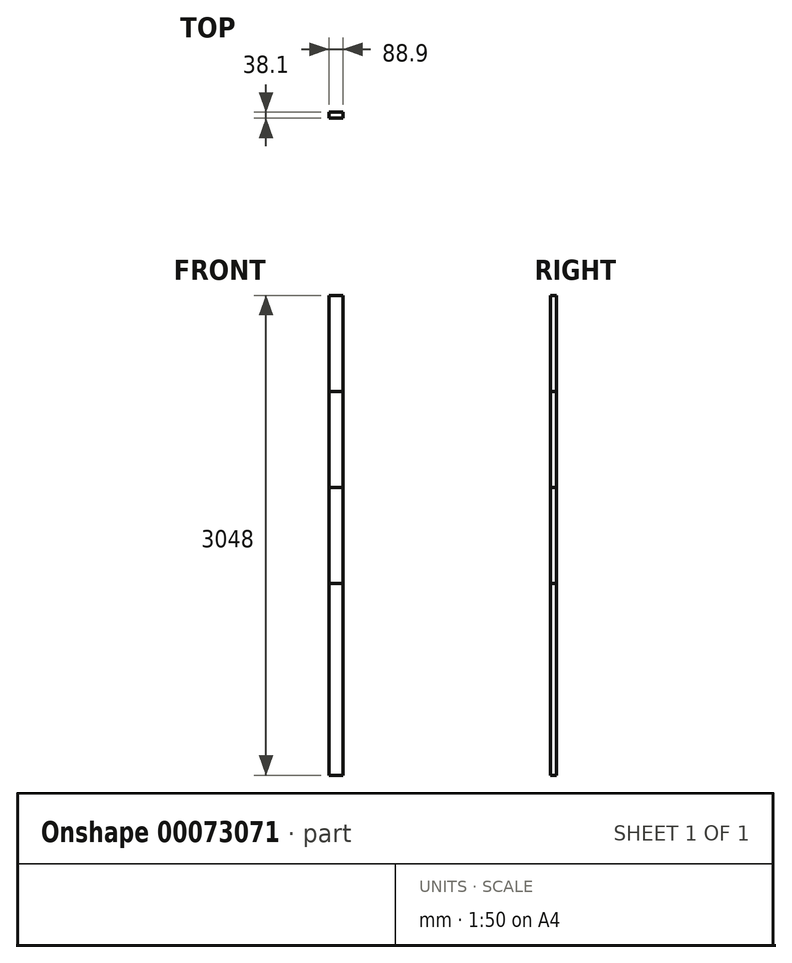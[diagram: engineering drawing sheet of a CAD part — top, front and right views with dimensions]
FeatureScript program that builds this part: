
annotation { "Feature Type Name" : "Feature", "Feature Type Description" : "" }
export const myFeature = defineFeature(function(context is Context, id is Id, definition is map)
    precondition{}
    {
        {
            var Q0;
            Q0=qCreatedBy(makeId("Top.planeOp"),FACE);
            var sketch = newSketch(context, id + "F0", { "sketchPlane" : qUnion([Q0])});
            skLineSegment(sketch, "E0.rect.bottom", {"start": v(44.45, -19.05) * mm, "end": v(-44.45, -19.05) * mm});
            skLineSegment(sketch, "E0.rect.top", {"start": v(44.45, 19.05) * mm, "end": v(-44.45, 19.05) * mm});
            skLineSegment(sketch, "E0.rect.left", {"start": v(44.45, -19.05) * mm, "end": v(44.45, 19.05) * mm});
            skLineSegment(sketch, "E0.rect.right", {"start": v(-44.45, -19.05) * mm, "end": v(-44.45, 19.05) * mm});
            skPoint(sketch, "E0.rect.middle", {"position": v(0, 0) * mm});
            skSolve(sketch);
        }
        {
            var Q0;
            Q0 = qSketchRegion(id + "F0", true);
            extrude(context, id + "F1", {"entities" : qUnion([Q0]), "depth" : 1219.2 * mm});
        }
        {
            var Q0;
            Q0=makeQuery(id+"F0.imprint","IMPRINT",FACE,{"disambiguationData":[TD([[makeQuery(id+"F0.imprint","IMPRINT",EDGE,{"derivedFrom":sQuery(id+"F0.wireOp",EDGE,"E0.rect.bottom")}),-1.0]])]});
            extrude(context, id + "F2", {"entities" : qUnion([Q0]), "depth" : 1828.8 * mm});
        }
        {
            var Q0;
            Q0 = qSketchRegion(id + "F0", true);
            extrude(context, id + "F3", {"entities" : qUnion([Q0]), "depth" : 2438.4 * mm});
        }
        {
            var Q0;
            Q0 = qSketchRegion(id + "F0", true);
            extrude(context, id + "F4", {"entities" : qUnion([Q0]), "depth" : 3048 * mm});
        }
    });
